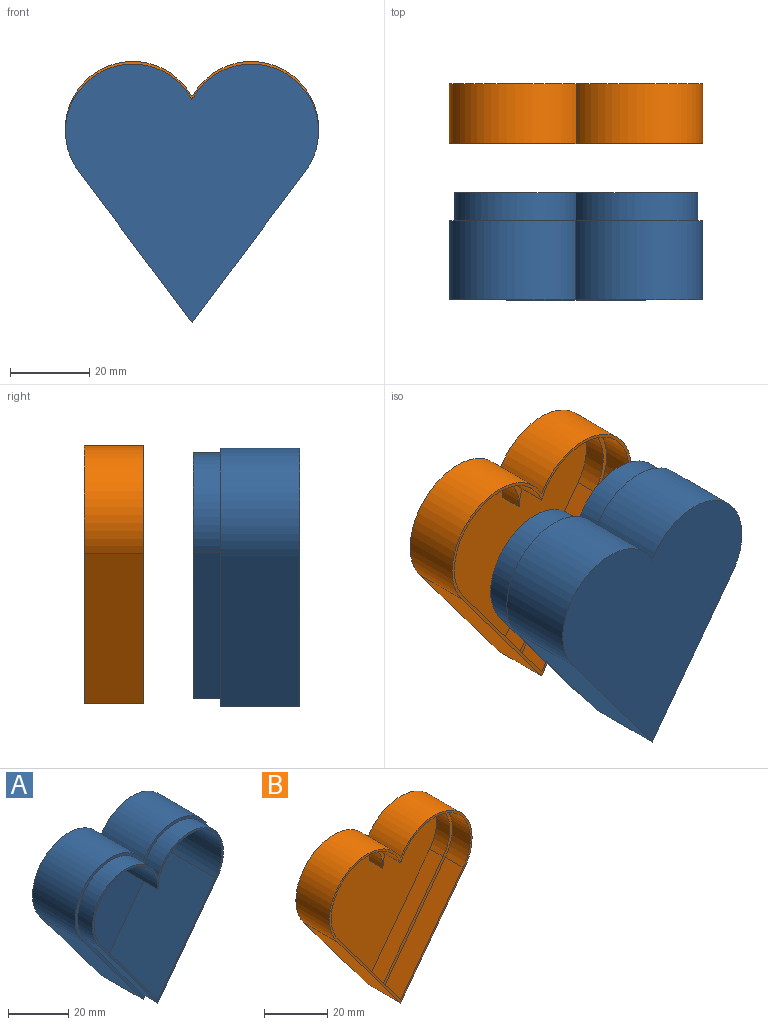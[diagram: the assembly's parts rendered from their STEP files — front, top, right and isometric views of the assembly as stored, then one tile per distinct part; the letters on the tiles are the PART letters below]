
ASSEMBLY  parts=2 mates=1
PART A: 16 faces, bbox 64x27x65.3 mm
  f0: plane 38.13x28.6mm, normal (-0.8,0,-0.6), area 953.3mm2, adj f1,f3,f4,f5
  f1: plane 38.13x28.6mm, normal (0.8,0,-0.6), area 953.3mm2, adj f0,f2,f4,f5
  f2: cylinder r=17mm len=32mm, axis (0,1,0), area 1120.3mm2, adj f1,f3,f4,f5
  f3: cylinder r=17mm len=32mm, axis (0,1,0), area 1120.3mm2, adj f0,f2,f4,f5
  f4: plane 65.33x64mm, normal (0,1,0), area 2607.6mm2, adj f0,f1,f2,f3
  f5: plane 65.33x64mm, normal (0,-1,0), area 245.2mm2, adj f0,f1,f2,f3,f6,f7,f8,f9
  f6: plane 36.85x27.64mm, normal (-0.8,0,-0.6), area 322.5mm2, adj f5,f7,f9,f14
  f7: plane 36.85x27.64mm, normal (0.8,0,-0.6), area 322.5mm2, adj f5,f6,f8,f14
  f8: cylinder r=15.8mm len=30.8mm, axis (0,1,0), area 383.3mm2, adj f5,f7,f9,f14
  f9: cylinder r=15.8mm len=30.8mm, axis (0,1,0), area 383.3mm2, adj f5,f6,f8,f14
  f10: plane 36x27mm, normal (-0.8,0,0.6), area 1170mm2, adj f11,f13,f14,f15
  f11: plane 36x27mm, normal (0.8,0,0.6), area 1170mm2, adj f10,f12,f14,f15
  f12: cylinder r=15mm len=30mm, axis (0,1,0), area 1476.2mm2, adj f11,f13,f14,f15
  f13: cylinder r=15mm len=30mm, axis (0,1,0), area 1476.2mm2, adj f10,f12,f14,f15
  f14: plane 62.13x61.6mm, normal (0,-1,0), area 160.8mm2, adj f6,f7,f8,f9,f10,f11,f12,f13
  f15: plane 60x60mm, normal (0,-1,0), area 2201.6mm2, adj f10,f11,f12,f13
PART B: 16 faces, bbox 64x15x65.3 mm
  f0: plane 38.13x28.6mm, normal (-0.8,0,-0.6), area 715mm2, adj f1,f3,f4,f9
  f1: plane 38.13x28.6mm, normal (0.8,0,-0.6), area 715mm2, adj f0,f2,f4,f9
  f2: cylinder r=17mm len=32mm, axis (0,1,0), area 840.3mm2, adj f1,f3,f4,f9
  f3: cylinder r=17mm len=32mm, axis (0,1,0), area 840.3mm2, adj f0,f2,f4,f9
  f4: plane 65.33x64mm, normal (0,1,0), area 2607.6mm2, adj f0,f1,f2,f3
  f5: cylinder r=16.2mm len=31.2mm, axis (0,1,0), area 440.4mm2, adj f6,f8,f9,f14
  f6: cylinder r=16.2mm len=31.2mm, axis (0,1,0), area 440.4mm2, adj f5,f7,f9,f14
  f7: plane 37.28x27.96mm, normal (-0.8,0,0.6), area 372.8mm2, adj f6,f8,f9,f14
  f8: plane 37.28x27.96mm, normal (0.8,0,0.6), area 372.8mm2, adj f5,f7,f9,f14
  f9: plane 65.33x64mm, normal (0,-1,0), area 164.2mm2, adj f0,f1,f2,f3,f5,f6,f7,f8
  f10: plane 36x27mm, normal (-0.8,0,0.6), area 270mm2, adj f11,f13,f14,f15
  f11: plane 36x27mm, normal (0.8,0,0.6), area 270mm2, adj f10,f12,f14,f15
  f12: cylinder r=15mm len=30mm, axis (0,1,0), area 340.7mm2, adj f11,f13,f14,f15
  f13: cylinder r=15mm len=30mm, axis (0,1,0), area 340.7mm2, adj f10,f12,f14,f15
  f14: plane 63.2x62.4mm, normal (0,-1,0), area 241.8mm2, adj f5,f6,f7,f8,f10,f11,f12,f13
  f15: plane 60x60mm, normal (0,-1,0), area 2201.6mm2, adj f10,f11,f12,f13
PLACE A rot(axis=(0,0,1),180deg) t=(10.82,-85.43,-21.14)mm
PLACE B t=(10.82,-30.87,-20.48)mm
MATE slider A.f14 <-> B.f14  axis (0,-1,0) through (10.82,-58.43,-67.48)mm
